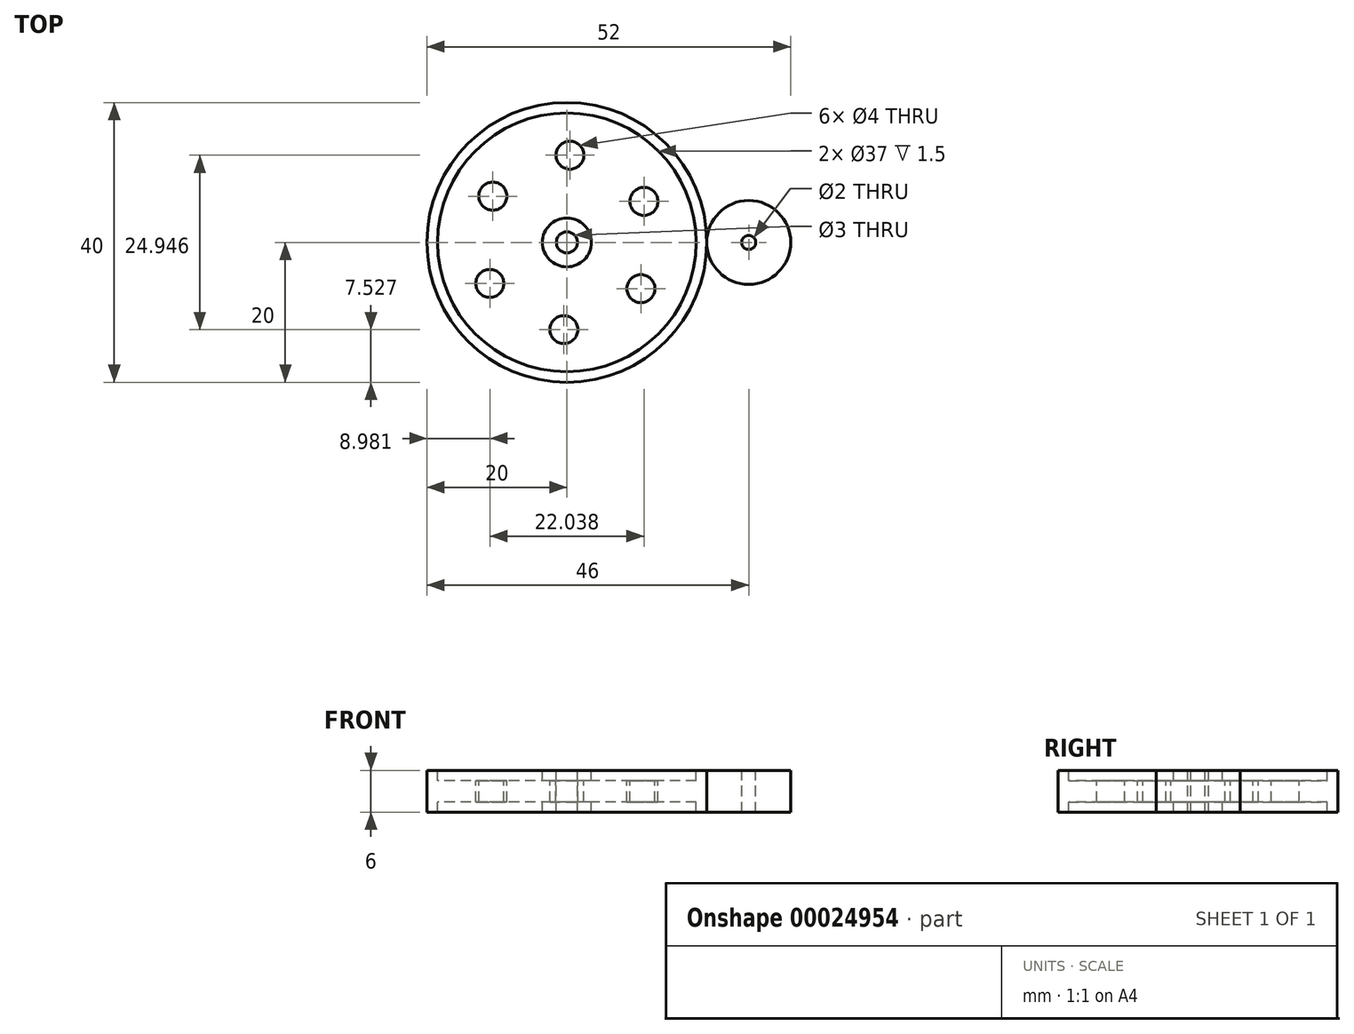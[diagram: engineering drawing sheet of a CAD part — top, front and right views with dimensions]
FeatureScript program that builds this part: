
annotation { "Feature Type Name" : "Feature", "Feature Type Description" : "" }
export const myFeature = defineFeature(function(context is Context, id is Id, definition is map)
    precondition{}
    {
        {
            var Q0;
            Q0=qCreatedBy(makeId("Front.planeOp"),FACE);
            var sketch = newSketch(context, id + "F0", { "sketchPlane" : qUnion([Q0])});
            skLineSegment(sketch, "E0.bottom", {"start": v(0, 0) * mm, "end": v(-15, 0) * mm});
            skLineSegment(sketch, "E0.top", {"start": v(0, 3) * mm, "end": v(-15, 3) * mm});
            skLineSegment(sketch, "E1.bottom", {"start": v(-15, 4.5) * mm, "end": v(-16.5, 4.5) * mm});
            skLineSegment(sketch, "E1.top", {"start": v(-15, -1.5) * mm, "end": v(-16.5, -1.5) * mm});
            skLineSegment(sketch, "E1.left", {"start": v(-15, 4.5) * mm, "end": v(-15, 3) * mm});
            skLineSegment(sketch, "E1.right", {"start": v(-16.5, 4.5) * mm, "end": v(-16.5, -1.5) * mm});
            skLineSegment(sketch, "E2.bottom", {"start": v(0, 4.5) * mm, "end": v(2, 4.5) * mm});
            skLineSegment(sketch, "E2.top", {"start": v(0, -1.5) * mm, "end": v(2, -1.5) * mm});
            skLineSegment(sketch, "E2.left", {"start": v(0, 4.5) * mm, "end": v(0, 3) * mm});
            skLineSegment(sketch, "E2.right", {"start": v(2, 4.5) * mm, "end": v(2, -1.5) * mm});
            skLineSegment(sketch, "E3", {"start": v(3.5, 17.27) * mm, "end": v(3.5, -9.4) * mm, "construction": true});
            skLineSegment(sketch, "E4", {"start": v(0, 0) * mm, "end": v(23.5, 0) * mm, "construction": true});
            skLineSegment(sketch, "E5.bottom", {"start": v(23.5, -1.5) * mm, "end": v(28.5, -1.5) * mm});
            skLineSegment(sketch, "E5.top", {"start": v(23.5, 4.5) * mm, "end": v(28.5, 4.5) * mm});
            skLineSegment(sketch, "E5.left", {"start": v(23.5, -1.5) * mm, "end": v(23.5, 4.5) * mm});
            skLineSegment(sketch, "E5.right", {"start": v(28.5, -1.5) * mm, "end": v(28.5, 4.5) * mm});
            skLineSegment(sketch, "E6", {"start": v(29.5, 7.66) * mm, "end": v(29.5, -8.96) * mm, "construction": true});
            skLineSegment(sketch, "E7.trimOffspring", {"start": v(-15, 0) * mm, "end": v(-15, -1.5) * mm});
            skLineSegment(sketch, "E8.trimOffspring", {"start": v(0, 0) * mm, "end": v(0, -1.5) * mm});
            skSolve(sketch);
        }
        {
            var Q0;
            {var subQ2=sQuery(id+"F0.wireOp",EDGE,"E0.bottom");Q0=makeQuery(id+"F0.imprint","IMPRINT",FACE,{"disambiguationData":[TD([[makeQuery(id+"F0.imprint","IMPRINT",EDGE,{"derivedFrom":subQ2}),-1.0]])]});}
            var Q1;
            {var subQ4=sQuery(id+"F0.wireOp",EDGE,"E1.bottom");Q1=makeQuery(id+"F0.imprint","IMPRINT",FACE,{"disambiguationData":[TD([[makeQuery(id+"F0.imprint","IMPRINT",EDGE,{"derivedFrom":subQ4}),1.0]])]});}
            var Q2;
            {var subQ4=sQuery(id+"F0.wireOp",EDGE,"E2.bottom");Q2=makeQuery(id+"F0.imprint","IMPRINT",FACE,{"disambiguationData":[TD([[makeQuery(id+"F0.imprint","IMPRINT",EDGE,{"derivedFrom":subQ4}),-1.0]])]});}
            var Q3;
            Q3=sQuery(id+"F0.wireOp",EDGE,"E3");
            revolve(context, id + "F1", {"entities" : qUnion([Q0, Q1, Q2]), "axis" : qUnion([Q3]), "revolveType" : RevolveType.FULL});
        }
        {
            var Q0;
            Q0=makeQuery(id+"F1.opRevolve","SWEPT_FACE",FACE,{"disambiguationData":[OSD([sQuery(id+"F0.wireOp",EDGE,"E0.top")])]});
            var sketch = newSketch(context, id + "F2", { "sketchPlane" : qUnion([Q0])});
            skCircle(sketch, "E9", {"center": v(3.93, 12.47) * mm, "radius": 2 * mm});
            skLineSegment(sketch, "E10", {"start": v(3.93, 12.47) * mm, "end": v(3.93, 3.47) * mm, "construction": true});
            skSolve(sketch);
        }
        {
            var Q0;
            Q0=makeQuery(id+"F2.imprint","IMPRINT",FACE,{"disambiguationData":[TD([[makeQuery(id+"F2.imprint","IMPRINT",EDGE,{"derivedFrom":sQuery(id+"F2.wireOp",EDGE,"E9")}),1.0]])]});
            extrude(context, id + "F3", {"entities" : qUnion([Q0]), "operationType" : NewBodyOperationType.REMOVE, "oppositeDirection" : true, "depth" : 254 * mm});
        }
        {
            var Q0;
            Q0=makeQuery(id+"F3.boolean.opBoolean","COPY",FACE,{"derivedFrom":makeQuery(id+"F3.opExtrude","SWEPT_FACE",FACE,{"disambiguationData":[OSD([sQuery(id+"F2.wireOp",EDGE,"E9")])]})});
            var Q1;
            Q1=makeQuery(id+"F1.opRevolve","SWEPT_FACE",FACE,{"disambiguationData":[OSD([sQuery(id+"F0.wireOp",EDGE,"E2.right")])]});
            circularPattern(context, id + "F4", {"faces" : qUnion([Q0]), "axis" : qUnion([Q1]), "angle" : 360 * degree, "instanceCount" : 6, "equalSpace" : true, "patternType" : PatternType.FACE});
        }
        {
            var Q0;
            Q0=makeQuery(id+"F0.imprint","IMPRINT",FACE,{"disambiguationData":[TD([[makeQuery(id+"F0.imprint","IMPRINT",EDGE,{"derivedFrom":sQuery(id+"F0.wireOp",EDGE,"E5.bottom")}),1.0]])]});
            var Q1;
            Q1=sQuery(id+"F0.wireOp",EDGE,"E6");
            revolve(context, id + "F5", {"entities" : qUnion([Q0]), "axis" : qUnion([Q1]), "revolveType" : RevolveType.FULL});
        }
    });
